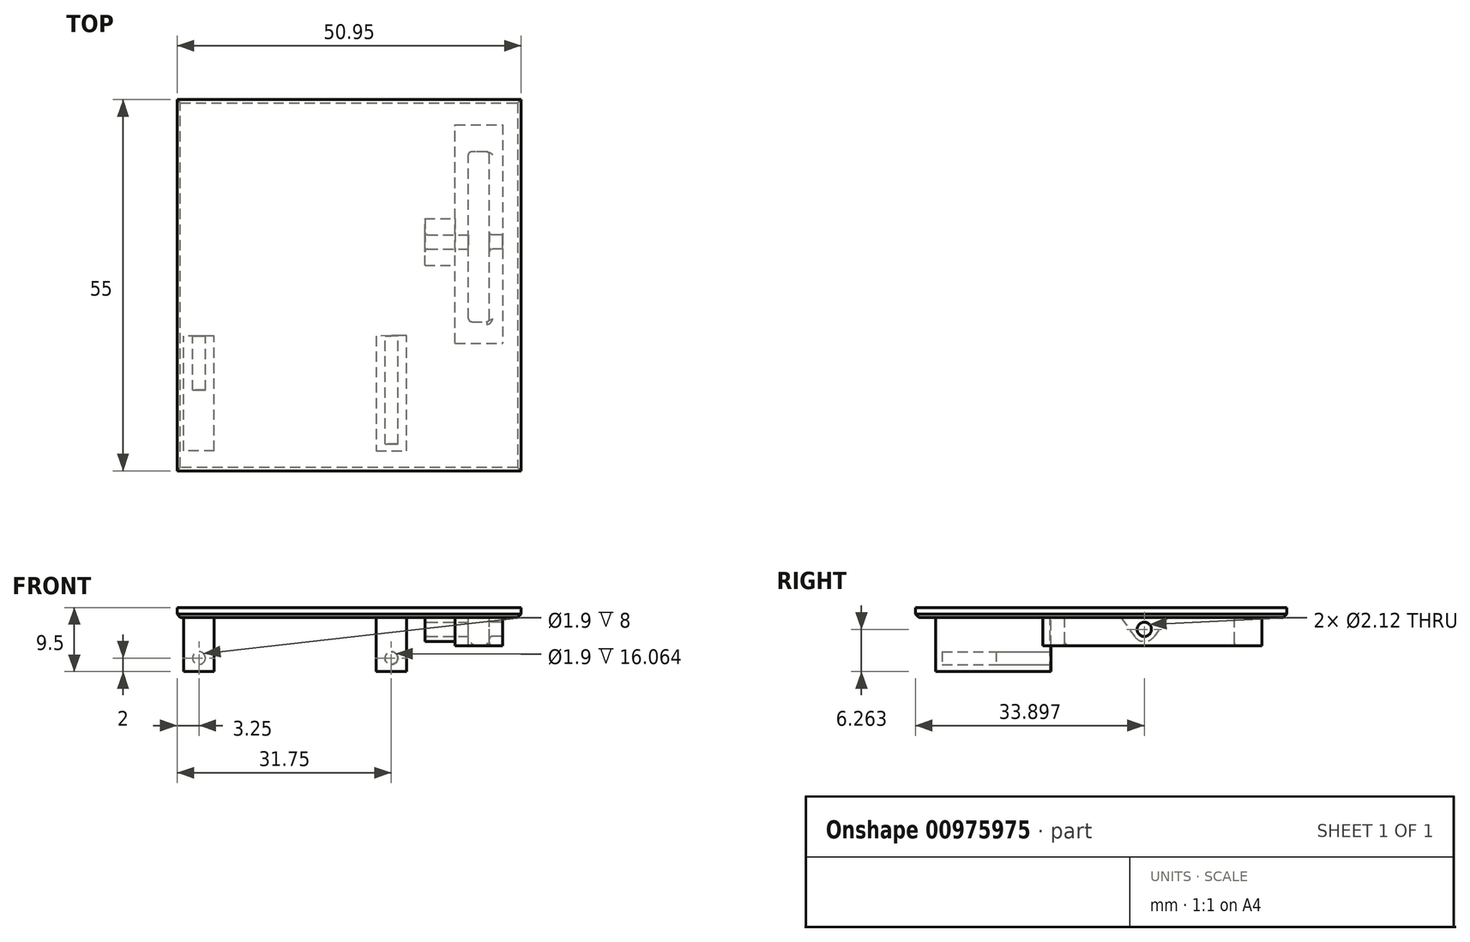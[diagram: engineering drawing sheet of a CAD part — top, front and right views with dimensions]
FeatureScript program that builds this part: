
annotation { "Feature Type Name" : "Feature", "Feature Type Description" : "" }
export const myFeature = defineFeature(function(context is Context, id is Id, definition is map)
    precondition{}
    {
        {
            var Q0;
            Q0=qCreatedBy(makeId("Front.planeOp"),FACE);
            var sketch = newSketch(context, id + "F0", { "sketchPlane" : qUnion([Q0])});
            skLineSegment(sketch, "E0.bottom", {"start": v(16.95, 0) * mm, "end": v(-34, 0) * mm});
            skLineSegment(sketch, "E0.top", {"start": v(16.95, 1.5) * mm, "end": v(-34, 1.5) * mm});
            skLineSegment(sketch, "E0.right", {"start": v(-34, 0) * mm, "end": v(-34, 1.5) * mm});
            skPoint(sketch, "E0.middle", {"position": v(0, 0.75) * mm});
            skLineSegment(sketch, "E1", {"start": v(16.95, 1.5) * mm, "end": v(16.95, 0) * mm});
            skPoint(sketch, "E0.left.end.orphan", {"position": v(34, 1.5) * mm});
            skPoint(sketch, "E2.orphan", {"position": v(34, 0) * mm});
            skSolve(sketch);
        }
        {
            var Q0;
            Q0=qCreatedBy(makeId("Top.planeOp"),FACE);
            var sketch = newSketch(context, id + "F1", { "sketchPlane" : qUnion([Q0])});
            skLineSegment(sketch, "E3", {"start": v(-28.5, -7.04) * mm, "end": v(-28.5, 9.96) * mm});
            skLineSegment(sketch, "E4", {"start": v(-28.5, 9.96) * mm, "end": v(-28.57, 9.96) * mm});
            skLineSegment(sketch, "E5", {"start": v(-4.5, 9.96) * mm, "end": v(-4.5, -7.04) * mm});
            skLineSegment(sketch, "E6", {"start": v(7.2, 19.34) * mm, "end": v(7.2, 28.67) * mm});
            skLineSegment(sketch, "E7", {"start": v(9.16, 28.67) * mm, "end": v(9.16, 19.34) * mm});
            skLineSegment(sketch, "E8", {"start": v(12.26, 19.44) * mm, "end": v(12.26, 28.66) * mm});
            skLineSegment(sketch, "E9", {"start": v(14.2, 28.6) * mm, "end": v(14.2, 19.38) * mm});
            skLineSegment(sketch, "E10", {"start": v(-33, -7.04) * mm, "end": v(-33, 9.96) * mm});
            skLineSegment(sketch, "E11", {"start": v(-33, 9.96) * mm, "end": v(-28.57, 9.96) * mm});
            skLineSegment(sketch, "E12", {"start": v(0, -7.04) * mm, "end": v(0, 10.05) * mm});
            skLineSegment(sketch, "E13", {"start": v(0, 10.05) * mm, "end": v(-4.5, 9.96) * mm});
            skLineSegment(sketch, "E14", {"start": v(-28.5, -7.04) * mm, "end": v(-33, -7.04) * mm});
            skLineSegment(sketch, "E15", {"start": v(-4.5, -7.04) * mm, "end": v(0, -7.04) * mm});
            skLineSegment(sketch, "E16", {"start": v(14.2, 19.38) * mm, "end": v(14.2, 8.9) * mm});
            skLineSegment(sketch, "E17", {"start": v(12.26, 12.1) * mm, "end": v(12.26, 19.44) * mm});
            skLineSegment(sketch, "E18", {"start": v(7.2, 19.34) * mm, "end": v(7.2, 8.9) * mm});
            skLineSegment(sketch, "E19", {"start": v(9.16, 12.1) * mm, "end": v(9.16, 19.34) * mm});
            skLineSegment(sketch, "E20", {"start": v(9.16, 28.67) * mm, "end": v(9.16, 37.25) * mm});
            skLineSegment(sketch, "E21", {"start": v(7.2, 28.67) * mm, "end": v(7.2, 41.3) * mm});
            skLineSegment(sketch, "E22", {"start": v(7.2, 41.3) * mm, "end": v(9.16, 41.3) * mm});
            skLineSegment(sketch, "E23", {"start": v(12.26, 28.66) * mm, "end": v(12.26, 37.25) * mm});
            skLineSegment(sketch, "E24", {"start": v(14.2, 41.2) * mm, "end": v(14.2, 28.6) * mm});
            skLineSegment(sketch, "E25", {"start": v(14.2, 41.2) * mm, "end": v(14.2, 37.25) * mm, "construction": true});
            skLineSegment(sketch, "E26", {"start": v(12.26, 37.25) * mm, "end": v(9.16, 37.25) * mm});
            skLineSegment(sketch, "E27", {"start": v(9.16, 41.3) * mm, "end": v(14.2, 41.3) * mm});
            skLineSegment(sketch, "E28", {"start": v(14.2, 41.3) * mm, "end": v(14.2, 41.2) * mm});
            skLineSegment(sketch, "E29", {"start": v(9.16, 12.1) * mm, "end": v(12.26, 12.1) * mm});
            skPoint(sketch, "E30.start.orphan", {"position": v(9.16, 13) * mm});
            skLineSegment(sketch, "E31", {"start": v(7.2, 8.9) * mm, "end": v(14.2, 8.9) * mm});
            skSolve(sketch);
        }
        {
            var Q0;
            Q0=makeQuery(id+"F1.imprint","IMPRINT",FACE,{"disambiguationData":[TD([[makeQuery(id+"F1.imprint","IMPRINT",EDGE,{"derivedFrom":sQuery(id+"F1.wireOp",EDGE,"E5")}),1.0]])]});
            var Q1;
            Q1=makeQuery(id+"F1.imprint","IMPRINT",FACE,{"disambiguationData":[TD([[makeQuery(id+"F1.imprint","IMPRINT",EDGE,{"derivedFrom":sQuery(id+"F1.wireOp",EDGE,"E3")}),1.0]])]});
            extrude(context, id + "F2", {"entities" : qUnion([Q0, Q1]), "oppositeDirection" : true, "depth" : 8 * mm, "offsetDistance" : 25 * mm});
        }
        {
            var Q0;
            Q0=makeQuery(id+"F1.imprint","IMPRINT",FACE,{"disambiguationData":[TD([[makeQuery(id+"F1.imprint","IMPRINT",EDGE,{"derivedFrom":sQuery(id+"F1.wireOp",EDGE,"E6")}),-1.0]])]});
            var Q1;
            Q1=makeQuery(id+"F1.imprint","IMPRINT",FACE,{"disambiguationData":[TD([[makeQuery(id+"F1.imprint","IMPRINT",EDGE,{"derivedFrom":sQuery(id+"F1.wireOp",EDGE,"E8")}),-1.0]])]});
            var Q2;
            {var subQ4=sQuery(id+"F1.wireOp",EDGE,"E22");Q2=makeQuery(id+"F1.imprint","IMPRINT",FACE,{"disambiguationData":[TD([[makeQuery(id+"F1.imprint","IMPRINT",EDGE,{"derivedFrom":subQ4}),-1.0]])]});}
            extrude(context, id + "F3", {"entities" : qUnion([Q0, Q1, Q2]), "operationType" : NewBodyOperationType.ADD, "oppositeDirection" : true, "depth" : 4.17 * mm, "offsetDistance" : 25 * mm});
        }
        {
            var Q0;
            Q0=makeQuery(id+"F0.imprint","IMPRINT",FACE,{"disambiguationData":[TD([[makeQuery(id+"F0.imprint","IMPRINT",EDGE,{"derivedFrom":sQuery(id+"F0.wireOp",EDGE,"E0.bottom")}),-1.0]])]});
            extrude(context, id + "F4", {"entities" : qUnion([Q0]), "operationType" : NewBodyOperationType.ADD, "depth" : 10 * mm, "offsetDistance" : 25 * mm, "hasSecondDirection" : true, "secondDirectionOppositeDirection" : true, "secondDirectionDepth" : 45 * mm});
        }
        {
            var Q0;
            Q0=makeQuery(id+"F3.opExtrude","SWEPT_FACE",FACE,{"disambiguationData":[OSD([sQuery(id+"F1.wireOp",EDGE,"E6"),sQuery(id+"F1.wireOp",EDGE,"E18")])]});
            var sketch = newSketch(context, id + "F5", { "sketchPlane" : qUnion([Q0])});
            skCircle(sketch, "E32", {"center": v(-23.9, -1.74) * mm, "radius": 1.06 * mm});
            skLineSegment(sketch, "E33.0", {"start": v(-9.96, -8) * mm, "end": v(-9.96, 0) * mm});
            skLineSegment(sketch, "E34.0", {"start": v(10, 0) * mm, "end": v(-45, 0) * mm});
            skArc(sketch, "E35", {"start": v(-23.88, 0.01) * mm, "mid": v(-23.9, 0.01) * mm, "end": v(-23.92, 0.01) * mm});
            skLineSegment(sketch, "E36", {"start": v(-23.92, 0.01) * mm, "end": v(-25.1, 0) * mm});
            skLineSegment(sketch, "E37", {"start": v(-23.9, 0) * mm, "end": v(-23.9, -1.74) * mm, "construction": true});
            skLineSegment(sketch, "E38.MirrorCS", {"start": v(-23.88, 0.01) * mm, "end": v(-22.7, 0) * mm});
            skArc(sketch, "E39.trimOffspring", {"start": v(-23.69, 0) * mm, "mid": v(-23.9, 0.01) * mm, "end": v(-24.1, 0) * mm});
            skLineSegment(sketch, "E40", {"start": v(-25.1, 0) * mm, "end": v(-22.7, 0) * mm});
            skCircle(sketch, "E41", {"center": v(-23.9, -1.74) * mm, "radius": 1.8 * mm});
            skLineSegment(sketch, "E42", {"start": v(-20.43, 0) * mm, "end": v(-22.43, -2.79) * mm});
            skLineSegment(sketch, "E43", {"start": v(-22.7, 0) * mm, "end": v(-20.43, 0) * mm});
            skLineSegment(sketch, "E44.MirrorCS", {"start": v(-27.36, 0) * mm, "end": v(-25.36, -2.79) * mm});
            skSolve(sketch);
        }
        {
            var Q0;
            Q0 = qSketchRegion(id + "F5", true);
            extrude(context, id + "F6", {"entities" : qUnion([Q0]), "operationType" : NewBodyOperationType.ADD, "depth" : 4.5 * mm, "offsetDistance" : 25 * mm});
        }
        {
            var Q0;
            Q0=makeQuery(id+"F6.boolean.opBoolean","SPLIT",FACE,{"disambiguationData":[TD([makeQuery(id+"F6.opExtrude","SWEPT_FACE",FACE,{"disambiguationData":[OSD([sQuery(id+"F5.wireOp",EDGE,"E32")])]})])],"derivedFrom":makeQuery(id+"F2.opExtrude","SWEPT_FACE",FACE,{"disambiguationData":[OSD([sQuery(id+"F1.wireOp",EDGE,"E6")])]})});
            var Q1;
            Q1=makeQuery(id+"F5.imprint","IMPRINT",FACE,{"disambiguationData":[TD([[makeQuery(id+"F5.imprint","IMPRINT",EDGE,{"derivedFrom":sQuery(id+"F5.wireOp",EDGE,"E32")}),1.0]])]});
            extrude(context, id + "F7", {"entities" : qUnion([Q0, Q1]), "operationType" : NewBodyOperationType.REMOVE, "endBound" : BoundingType.THROUGH_ALL, "oppositeDirection" : true, "depth" : 25 * mm, "offsetDistance" : 25 * mm});
        }
        {
            var Q0;
            Q0=makeQuery(id+"F2.opExtrude","SWEPT_FACE",FACE,{"disambiguationData":[OSD([sQuery(id+"F1.wireOp",EDGE,"E4"),sQuery(id+"F1.wireOp",EDGE,"E11")])]});
            var sketch = newSketch(context, id + "F8", { "sketchPlane" : qUnion([Q0])});
            skCircle(sketch, "E45", {"center": v(30.75, -6) * mm, "radius": 0.95 * mm});
            skPoint(sketch, "E46", {"position": v(30.75, 0) * mm});
            skLineSegment(sketch, "E47.0", {"start": v(28.5, -8) * mm, "end": v(28.5, 0) * mm});
            skPoint(sketch, "E48.0", {"position": v(2.25, 0) * mm});
            skLineSegment(sketch, "E49.0", {"start": v(4.5, -8) * mm, "end": v(4.5, 0) * mm});
            skCircle(sketch, "E50", {"center": v(2.25, -6) * mm, "radius": 0.95 * mm});
            skSolve(sketch);
        }
        {
            var Q0;
            Q0=makeQuery(id+"F8.imprint","IMPRINT",FACE,{"disambiguationData":[TD([[makeQuery(id+"F8.imprint","IMPRINT",EDGE,{"derivedFrom":sQuery(id+"F8.wireOp",EDGE,"E45")}),1.0]])]});
            var Q1;
            Q1=makeQuery(id+"F8.imprint","IMPRINT",FACE,{"disambiguationData":[TD([[makeQuery(id+"F8.imprint","IMPRINT",EDGE,{"derivedFrom":sQuery(id+"F8.wireOp",EDGE,"E50")}),1.0]])]});
            extrude(context, id + "F9", {"entities" : qUnion([Q0, Q1]), "operationType" : NewBodyOperationType.REMOVE, "oppositeDirection" : true, "depth" : 8 * mm, "offsetDistance" : 25 * mm});
        }
        {
            var Q0;
            Q0=makeQuery(id+"F9.boolean.opBoolean","COPY",FACE,{"derivedFrom":makeQuery(id+"F9.opExtrude","CAP_FACE",FACE,{"disambiguationData":[OSD([sQuery(id+"F8.wireOp",EDGE,"E50")])],"isStart":false})});
            extrude(context, id + "F10", {"entities" : qUnion([Q0]), "operationType" : NewBodyOperationType.REMOVE, "oppositeDirection" : true, "depth" : 8 * mm, "offsetDistance" : 25 * mm, "hasSecondDirection" : true, "secondDirectionOppositeDirection" : false, "secondDirectionDepth" : 25 * mm});
        }
        {
            var Q0;
            Q0=makeQuery(id+"F4.opExtrude","CAP_EDGE",EDGE,{"disambiguationData":[OSD([sQuery(id+"F0.wireOp",EDGE,"E0.bottom")])],"isStart":true});
            var Q1;
            Q1=makeQuery(id+"F4.opExtrude","SWEPT_EDGE",EDGE,{"disambiguationData":[OSD([sQuery(id+"F0.wireOp",EDGE,"E0.bottom"),sQuery(id+"F0.wireOp",EDGE,"E0.right")])]});
            var Q2;
            Q2=makeQuery(id+"F4.opExtrude","CAP_EDGE",EDGE,{"disambiguationData":[OSD([sQuery(id+"F0.wireOp",EDGE,"E0.bottom")])],"isStart":false});
            var Q3;
            Q3=makeQuery(id+"F4.opExtrude","SWEPT_EDGE",EDGE,{"disambiguationData":[OSD([sQuery(id+"F0.wireOp",EDGE,"E0.bottom"),sQuery(id+"F0.wireOp",EDGE,"E1")])]});
            chamfer(context, id + "F11", {"entities" : qUnion([Q0, Q1, Q2, Q3]), "width" : 0.5 * mm, "tangentPropagation" : true});
        }
        {
            var Q0;
            Q0=makeQuery(id+"F3.opExtrude","SWEPT_EDGE",EDGE,{"disambiguationData":[OSD([sQuery(id+"F1.wireOp",EDGE,"ANL60HPb-0yGG-vL8i-m0in-P9sS61fbuNCe"),sQuery(id+"F1.wireOp",EDGE,"E7")])]});
            var Q1;
            Q1=makeQuery(id+"F3.opExtrude","SWEPT_EDGE",EDGE,{"disambiguationData":[OSD([sQuery(id+"F1.wireOp",EDGE,"E8"),sQuery(id+"F1.wireOp",EDGE,"4xifEalK-b8Zi-sANQ-kgEv-l2afLqo77SnV")])]});
            var Q2;
            Q2=makeQuery(id+"F3.opExtrude","SWEPT_EDGE",EDGE,{"disambiguationData":[OSD([sQuery(id+"F1.wireOp",EDGE,"E19"),sQuery(id+"F1.wireOp",EDGE,"T4rK8h2W-o50D-atop-BnAV-5Gmrk1dhfltF")])]});
            var Q3;
            Q3=makeQuery(id+"F3.opExtrude","CAP_EDGE",EDGE,{"disambiguationData":[OSD([sQuery(id+"F1.wireOp",EDGE,"E17")])],"isStart":false});
            var Q4;
            Q4=makeQuery(id+"F3.opExtrude","CAP_EDGE",EDGE,{"disambiguationData":[OSD([sQuery(id+"F1.wireOp",EDGE,"E8")])],"isStart":false});
            var Q5;
            Q5=makeQuery(id+"F3.opExtrude","CAP_EDGE",EDGE,{"disambiguationData":[OSD([sQuery(id+"F1.wireOp",EDGE,"aDVc1Znh-qNZX-8fZF-ib5m-liXtoZwzs1Gb")])],"isStart":false});
            fillet(context, id + "F12", {"entities" : qUnion([Q0, Q1, Q2, Q3, Q4, Q5]), "radius" : .5 * mm, "tangentPropagation" : true, "allowEdgeOverflow" : false});
        }
        {
            var Q0;
            Q0=makeQuery(id+"F7.boolean.opBoolean","INTERSECT",EDGE,{"derivedFrom":[makeQuery(id+"F3.opExtrude","SWEPT_FACE",FACE,{"disambiguationData":[OSD([sQuery(id+"F1.wireOp",EDGE,"E8"),sQuery(id+"F1.wireOp",EDGE,"E17"),sQuery(id+"F1.wireOp",EDGE,"E23")])]}),makeQuery(id+"F7.opExtrude","SWEPT_FACE",FACE,{"disambiguationData":[OSD([sQuery(id+"F5.wireOp",EDGE,"E32")])]})]});
            var Q1;
            Q1=makeQuery(id+"F6.opExtrude","CAP_EDGE",EDGE,{"disambiguationData":[OSD([sQuery(id+"F5.wireOp",EDGE,"E32")])],"isStart":false});
            var Q2;
            Q2=makeQuery(id+"F3.opExtrude","CAP_EDGE",EDGE,{"disambiguationData":[OSD([sQuery(id+"F1.wireOp",EDGE,"E7"),sQuery(id+"F1.wireOp",EDGE,"E19"),sQuery(id+"F1.wireOp",EDGE,"E20")])],"isStart":false});
            var Q3;
            {var subQ0=sQuery(id+"F1.wireOp",EDGE,"E23");var subQ1=sQuery(id+"F1.wireOp",EDGE,"E17");var subQ2=sQuery(id+"F1.wireOp",EDGE,"E8");Q3=makeQuery(id+"F12.opFillet","BLEND_EDGE",EDGE,{"blendedFrom":[makeQuery(id+"F3.opExtrude","CAP_EDGE",EDGE,{"disambiguationData":[OSD([subQ2,subQ1,subQ0])],"isStart":false}),makeQuery(id+"F3.opExtrude","CAP_FACE",FACE,{"disambiguationData":[OSD([sQuery(id+"F1.wireOp",EDGE,"E6"),sQuery(id+"F1.wireOp",EDGE,"E7"),subQ2,sQuery(id+"F1.wireOp",EDGE,"E9"),sQuery(id+"F1.wireOp",EDGE,"E16"),subQ1,sQuery(id+"F1.wireOp",EDGE,"E18"),sQuery(id+"F1.wireOp",EDGE,"E19"),sQuery(id+"F1.wireOp",EDGE,"E20"),sQuery(id+"F1.wireOp",EDGE,"E21"),sQuery(id+"F1.wireOp",EDGE,"E22"),subQ0,sQuery(id+"F1.wireOp",EDGE,"E24"),sQuery(id+"F1.wireOp",EDGE,"E26"),sQuery(id+"F1.wireOp",EDGE,"E27"),sQuery(id+"F1.wireOp",EDGE,"E28"),sQuery(id+"F1.wireOp",EDGE,"E29"),sQuery(id+"F1.wireOp",EDGE,"E31")])],"isStart":false})],"blendedInto":[makeQuery(id+"F3.opExtrude","CAP_FACE",FACE,{"disambiguationData":[OSD([sQuery(id+"F1.wireOp",EDGE,"E6"),sQuery(id+"F1.wireOp",EDGE,"E7"),subQ2,sQuery(id+"F1.wireOp",EDGE,"E9"),sQuery(id+"F1.wireOp",EDGE,"E16"),subQ1,sQuery(id+"F1.wireOp",EDGE,"E18"),sQuery(id+"F1.wireOp",EDGE,"E19"),sQuery(id+"F1.wireOp",EDGE,"E20"),sQuery(id+"F1.wireOp",EDGE,"E21"),sQuery(id+"F1.wireOp",EDGE,"E22"),subQ0,sQuery(id+"F1.wireOp",EDGE,"E24"),sQuery(id+"F1.wireOp",EDGE,"E26"),sQuery(id+"F1.wireOp",EDGE,"E27"),sQuery(id+"F1.wireOp",EDGE,"E28"),sQuery(id+"F1.wireOp",EDGE,"E29"),sQuery(id+"F1.wireOp",EDGE,"E31")])],"isStart":false})]});}
            var Q4;
            Q4=makeQuery(id+"F3.opExtrude","SWEPT_EDGE",EDGE,{"disambiguationData":[OSD([sQuery(id+"F1.wireOp",EDGE,"E17"),sQuery(id+"F1.wireOp",EDGE,"E29")])]});
            var Q5;
            Q5=makeQuery(id+"F3.opExtrude","SWEPT_EDGE",EDGE,{"disambiguationData":[OSD([sQuery(id+"F1.wireOp",EDGE,"E20"),sQuery(id+"F1.wireOp",EDGE,"E26")])]});
            var Q6;
            Q6=makeQuery(id+"F3.opExtrude","SWEPT_EDGE",EDGE,{"disambiguationData":[OSD([sQuery(id+"F1.wireOp",EDGE,"E23"),sQuery(id+"F1.wireOp",EDGE,"E26")])]});
            fillet(context, id + "F13", {"entities" : qUnion([Q0, Q1, Q2, Q3, Q4, Q5, Q6]), "radius" : 0.4 * mm, "tangentPropagation" : true, "allowEdgeOverflow" : false});
        }
    });
